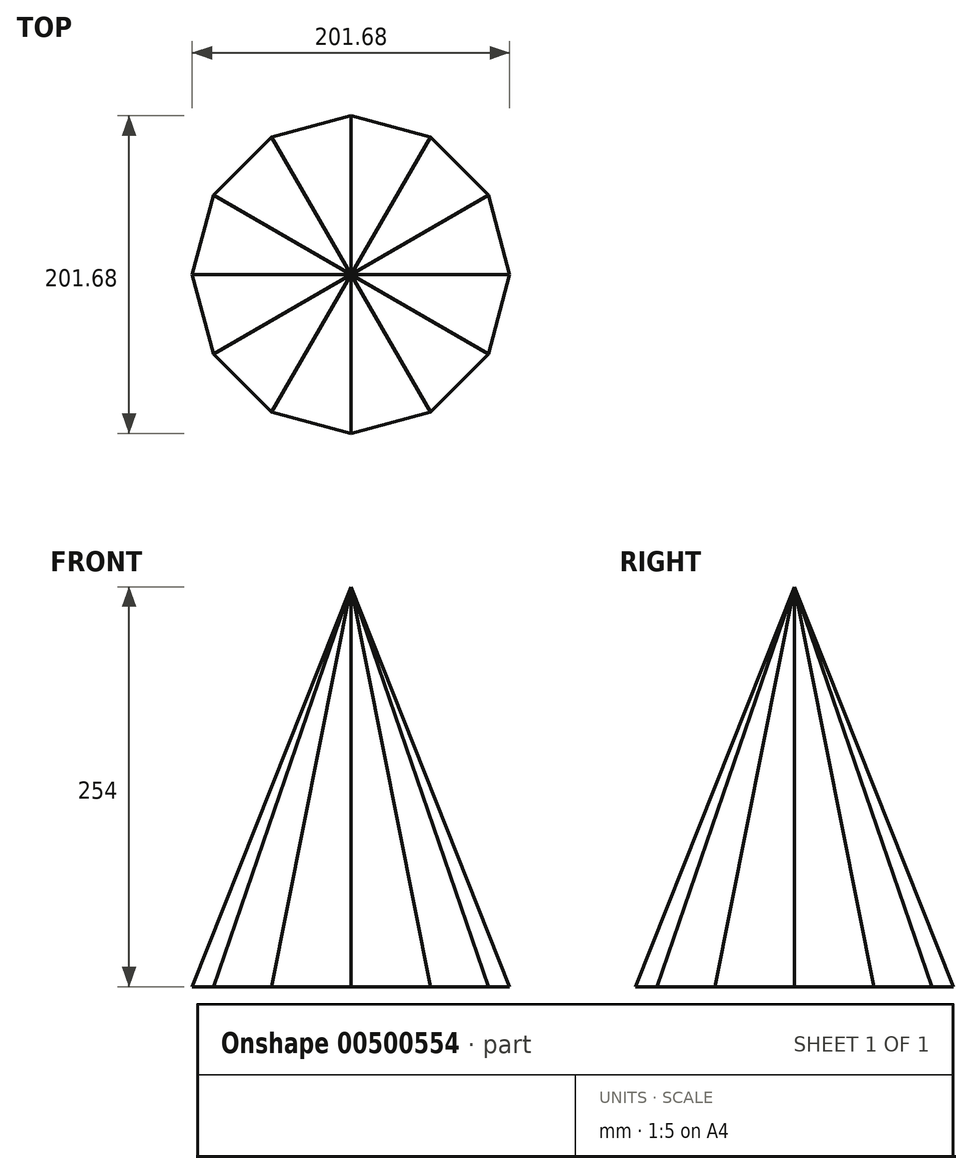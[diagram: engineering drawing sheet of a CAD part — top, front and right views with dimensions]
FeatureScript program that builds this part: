
annotation { "Feature Type Name" : "Feature", "Feature Type Description" : "" }
export const myFeature = defineFeature(function(context is Context, id is Id, definition is map)
    precondition{}
    {
        {
            var Q0;
            Q0=qCreatedBy(makeId("Top.planeOp"),FACE);
            var sketch = newSketch(context, id + "F0", { "sketchPlane" : qUnion([Q0])});
            skCircle(sketch, "E0.cCircle", {"center": v(0, 0) * mm, "radius": 100.84 * mm, "construction": true});
            skLineSegment(sketch, "E0.0", {"start": v(0, 100.84) * mm, "end": v(50.42, 87.33) * mm});
            skLineSegment(sketch, "E0.1", {"start": v(50.42, 87.33) * mm, "end": v(87.33, 50.42) * mm});
            skLineSegment(sketch, "E0.2", {"start": v(87.33, 50.42) * mm, "end": v(100.84, 0) * mm});
            skLineSegment(sketch, "E0.3", {"start": v(100.84, 0) * mm, "end": v(87.33, -50.42) * mm});
            skLineSegment(sketch, "E0.4", {"start": v(87.33, -50.42) * mm, "end": v(50.42, -87.33) * mm});
            skLineSegment(sketch, "E0.5", {"start": v(50.42, -87.33) * mm, "end": v(0, -100.84) * mm});
            skLineSegment(sketch, "E0.6", {"start": v(0, -100.84) * mm, "end": v(-50.42, -87.33) * mm});
            skLineSegment(sketch, "E0.7", {"start": v(-50.42, -87.33) * mm, "end": v(-87.33, -50.42) * mm});
            skLineSegment(sketch, "E0.8", {"start": v(-87.33, -50.42) * mm, "end": v(-100.84, 0) * mm});
            skLineSegment(sketch, "E0.9", {"start": v(-100.84, 0) * mm, "end": v(-87.33, 50.42) * mm});
            skLineSegment(sketch, "E0.10", {"start": v(-87.33, 50.42) * mm, "end": v(-50.42, 87.33) * mm});
            skLineSegment(sketch, "E0.11", {"start": v(-50.42, 87.33) * mm, "end": v(0, 100.84) * mm});
            skSolve(sketch);
        }
        {
            var Q0;
            Q0=qCreatedBy(makeId("Top.planeOp"),FACE);
            cPlane(context, id + "F1", {"entities" : qUnion([Q0]), "cplaneType" : CPlaneType.OFFSET, "offset" : 254 * mm, "width" : 152.4 * mm, "height" : 152.4 * mm});
        }
        {
            var Q0;
            Q0=qCreatedBy(id+"F1.planeOp",FACE);
            var sketch = newSketch(context, id + "F2", { "sketchPlane" : qUnion([Q0])});
            skPoint(sketch, "E1", {"position": v(0, 0) * mm});
            skSolve(sketch);
        }
        {
            var Q0;
            Q0=makeQuery(id+"F0.imprint","IMPRINT",FACE,{"disambiguationData":[TD([[makeQuery(id+"F0.imprint","IMPRINT",EDGE,{"derivedFrom":sQuery(id+"F0.wireOp",EDGE,"E0.0")}),-1.0]])]});
            var Q1;
            Q1=sQuery(id+"F2.wireOp",VERTEX,"E1");
            loft(context, id + "F3", {"sheetProfilesArray" : [{ "sheetProfileEntities" : qUnion([Q0]) }, { "sheetProfileEntities" : qUnion([Q1]) }]});
        }
    });
